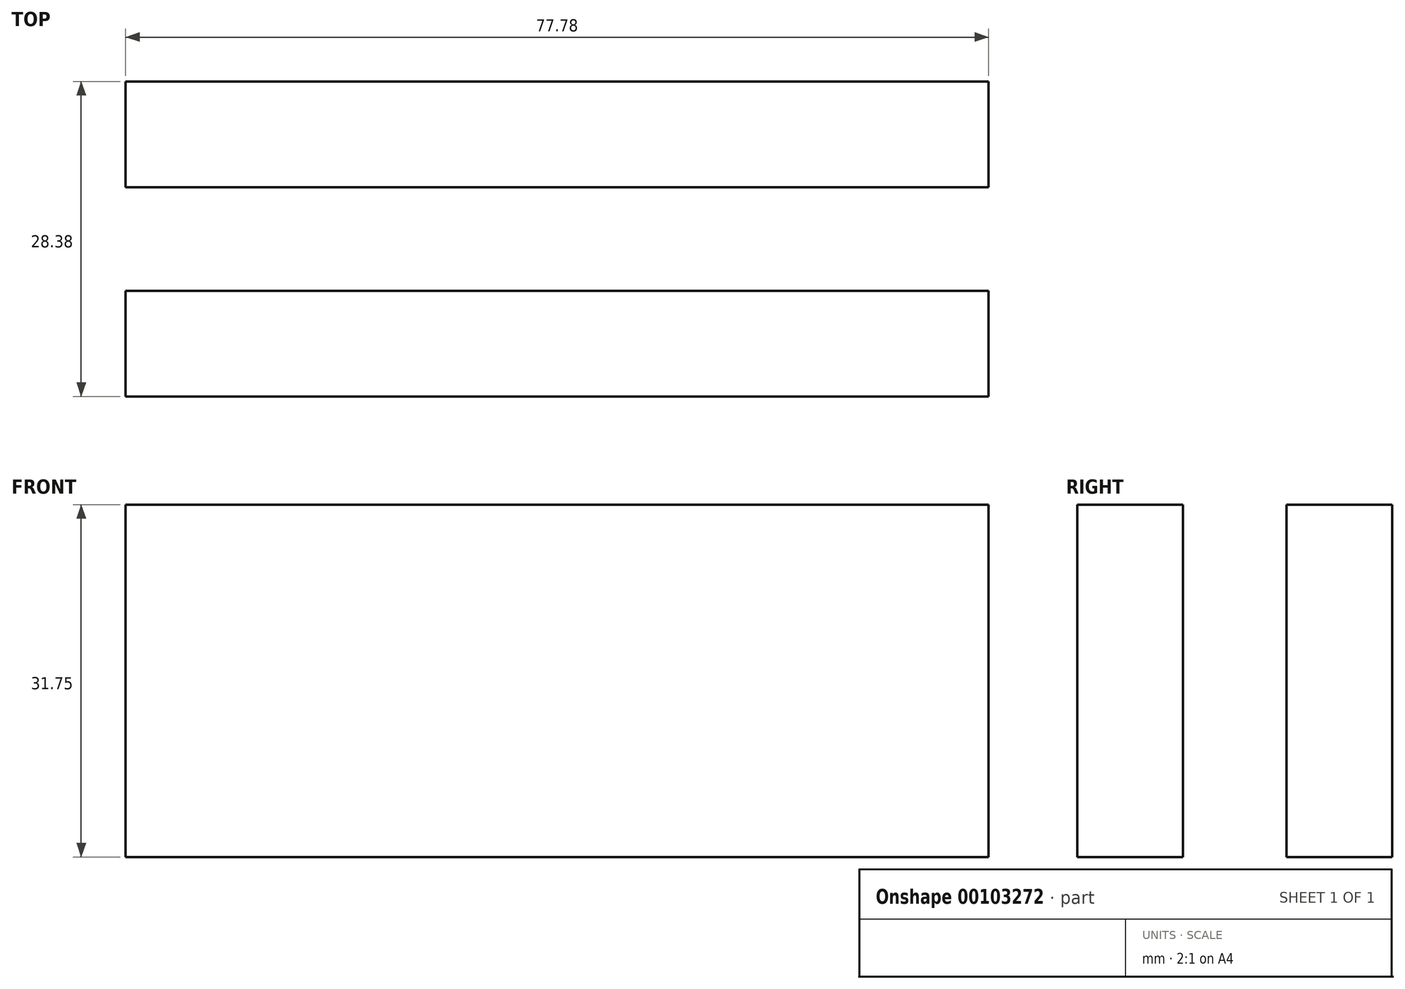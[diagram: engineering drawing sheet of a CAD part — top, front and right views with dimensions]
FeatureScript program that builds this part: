
annotation { "Feature Type Name" : "Feature", "Feature Type Description" : "" }
export const myFeature = defineFeature(function(context is Context, id is Id, definition is map)
    precondition{}
    {
        {
            var Q0;
            Q0=qCreatedBy(makeId("Top.planeOp"),FACE);
            var sketch = newSketch(context, id + "F0", { "sketchPlane" : qUnion([Q0])});
            skLineSegment(sketch, "E0.bottom", {"start": v(-36.77, 27.01) * mm, "end": v(41.01, 27.01) * mm});
            skLineSegment(sketch, "E0.top", {"start": v(-36.77, 17.49) * mm, "end": v(41.01, 17.49) * mm});
            skLineSegment(sketch, "E0.left", {"start": v(-36.77, 27.01) * mm, "end": v(-36.77, 17.49) * mm});
            skLineSegment(sketch, "E0.right", {"start": v(41.01, 27.01) * mm, "end": v(41.01, 17.49) * mm});
            skLineSegment(sketch, "E1.bottom", {"start": v(-36.77, 45.87) * mm, "end": v(41.01, 45.87) * mm});
            skLineSegment(sketch, "E1.top", {"start": v(-36.77, 36.34) * mm, "end": v(41.01, 36.34) * mm});
            skLineSegment(sketch, "E1.left", {"start": v(-36.77, 45.87) * mm, "end": v(-36.77, 36.34) * mm});
            skLineSegment(sketch, "E1.right", {"start": v(41.01, 45.87) * mm, "end": v(41.01, 36.34) * mm});
            skSolve(sketch);
        }
        {
            var Q0;
            Q0=makeQuery(id+"F0.imprint","IMPRINT",FACE,{"disambiguationData":[TD([[makeQuery(id+"F0.imprint","IMPRINT",EDGE,{"derivedFrom":sQuery(id+"F0.wireOp",EDGE,"E1.bottom")}),-1.0]])]});
            var Q1;
            Q1=makeQuery(id+"F0.imprint","IMPRINT",FACE,{"disambiguationData":[TD([[makeQuery(id+"F0.imprint","IMPRINT",EDGE,{"derivedFrom":sQuery(id+"F0.wireOp",EDGE,"E0.bottom")}),-1.0]])]});
            extrude(context, id + "F1", {"entities" : qUnion([Q0, Q1]), "depth" : 31.75 * mm});
        }
    });
